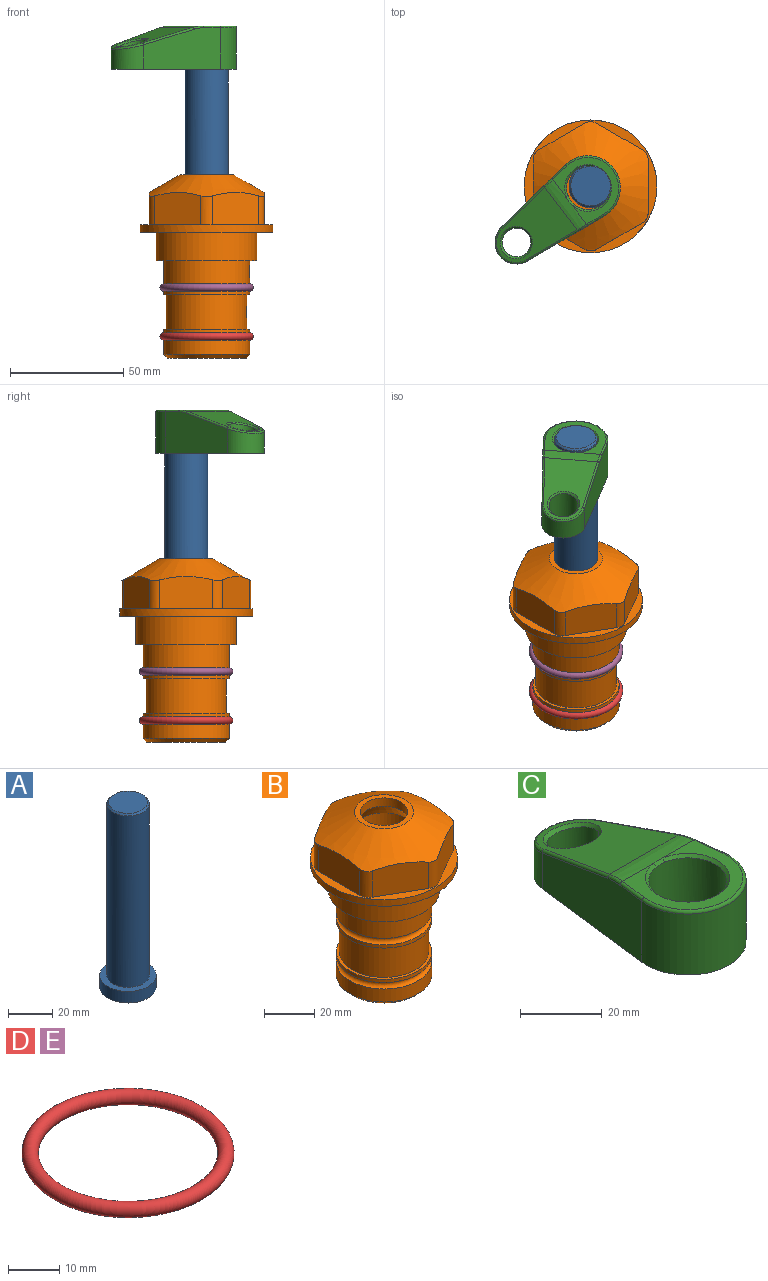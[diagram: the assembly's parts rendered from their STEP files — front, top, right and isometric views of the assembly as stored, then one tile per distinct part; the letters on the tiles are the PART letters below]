
ASSEMBLY  parts=5 mates=4
PART A: 6 faces, bbox 25.4x25.4x101.6 mm
  f0: plane 17.46x17.46mm, normal (0,0,1), area 239.5mm2, adj f5
  f1: plane 25.4x25.4mm, normal (0,0,-1), area 506.7mm2, adj f2
  f2: cylinder r=12.7mm len=25.4mm, axis (0,0,1), area 506.7mm2, adj f1,f3
  f3: plane 25.4x25.4mm, normal (0,0,1), area 221.7mm2, adj f2,f4
  f4: cylinder r=9.53mm len=94.46mm, axis (0,0,1), area 5653mm2, adj f3,f5
  f5: cone r=8.73mm half-angle=45deg, axis (0,0,-1), area 64.4mm2, adj f0,f4
PART B: 36 faces, bbox 58.7x58.7x81 mm
  f0: cylinder r=17.78mm len=35.56mm, axis (0,0,1), area 1670.8mm2, adj f23,f24,f31
  f1: cylinder r=19.05mm len=38.1mm, axis (0,0,1), area 1191.9mm2, adj f26,f27,f30
  f2: plane 58.66x58.66mm, normal (0,0,-1), area 1150.6mm2, adj f3,f28
  f3: cylinder r=29.33mm len=58.66mm, axis (0,0,-1), area 585.1mm2, adj f2,f4
  f4: plane 58.66x58.66mm, normal (0,0,1), area 475.9mm2, adj f3,f5,f6,f7,f8,f9,f10,f11
  f5: plane 20.32x14.34mm, normal (-0.5,0.87,0), area 324.4mm2, adj f4,f15,f16,f17
  f6: plane 20.32x14.34mm, normal (0.5,0.87,0), area 324.4mm2, adj f4,f14,f15,f17
  f7: plane 23.48x14.34mm, normal (1,0,0), area 324.4mm2, adj f4,f13,f14,f17
  f8: plane 20.32x14.34mm, normal (0.5,-0.87,0), area 324.4mm2, adj f4,f12,f13,f17
  f9: plane 20.32x14.34mm, normal (-0.5,-0.87,0), area 324.4mm2, adj f4,f11,f12,f17
  f10: plane 23.48x14.34mm, normal (-1,0,0), area 324.4mm2, adj f4,f11,f16,f17
  f11: cylinder r=5.08mm len=12.85mm, axis (0,0,-1), area 67.2mm2, adj f4,f9,f10,f17
  f12: cylinder r=5.08mm len=12.85mm, axis (0,0,-1), area 67.2mm2, adj f4,f8,f9,f17
  f13: cylinder r=5.08mm len=12.85mm, axis (0,0,-1), area 67.2mm2, adj f4,f7,f8,f17
  f14: cylinder r=5.08mm len=12.85mm, axis (0,0,-1), area 67.2mm2, adj f4,f6,f7,f17
  f15: cylinder r=5.08mm len=12.85mm, axis (0,0,-1), area 67.2mm2, adj f4,f5,f6,f17
  f16: cylinder r=5.08mm len=12.85mm, axis (0,0,-1), area 67.2mm2, adj f4,f5,f10,f17
  f17: cone r=11.73mm half-angle=60deg, axis (0,0,-1), area 2071.8mm2, adj f5,f6,f7,f8,f9,f10,f11,f12
  f18: plane 23.46x23.46mm, normal (0,0,1), area 147.4mm2, adj f17,f35
  f19: plane 34.93x34.93mm, normal (0,0,-1), area 958mm2, adj f29
  f20: cylinder r=19.05mm len=38.1mm, axis (0,0,1), area 760.1mm2, adj f21,f29
  f21: torus R=19.05mm, axis (0,0,1), area 565.3mm2, adj f20,f22
  f22: cylinder r=19.05mm len=38.1mm, axis (0,0,1), area 190mm2, adj f21,f23
  f23: plane 38.1x38.1mm, normal (0,0,1), area 146.9mm2, adj f0,f22
  f24: plane 38.1x38.1mm, normal (0,0,-1), area 146.9mm2, adj f0,f25
  f25: cylinder r=19.05mm len=38.1mm, axis (0,0,1), area 190mm2, adj f24,f26
  f26: torus R=19.05mm, axis (0,0,1), area 565.3mm2, adj f1,f25
  f27: plane 44.45x44.45mm, normal (0,0,-1), area 411.7mm2, adj f1,f28
  f28: cylinder r=22.23mm len=44.45mm, axis (0,0,1), area 1773.5mm2, adj f2,f27
  f29: cone r=19.05mm half-angle=45deg, axis (0,0,1), area 257.5mm2, adj f19,f20
  f30: cylinder r=3.17mm len=6.75mm, axis (-1,0,0), area 128mm2, adj f1,f33
  f31: cylinder r=3.17mm len=6.35mm, axis (-1,0,0), area 102.5mm2, adj f0,f33
  f32: plane 25.4x25.4mm, normal (0,0,1), area 506.7mm2, adj f33
  f33: cylinder r=12.7mm len=66.42mm, axis (0,0,-1), area 5236.2mm2, adj f30,f31,f32,f34
  f34: cone r=9.53mm half-angle=30deg, axis (0,0,-1), area 443.4mm2, adj f33,f35
  f35: cylinder r=9.53mm len=19.05mm, axis (0,0,-1), area 240.9mm2, adj f18,f34
PART C: 31 faces, bbox 31.7x65.5x19.8 mm
  f0: plane 39.12x18.26mm, normal (0.99,0.12,0), area 612.2mm2, adj f1,f4,f7,f11,f13,f15
  f1: cylinder r=9.53mm len=18.91mm, axis (0,0,-1), area 296.1mm2, adj f0,f2,f7,f17
  f2: plane 39.12x18.26mm, normal (-0.99,0.12,0), area 612.2mm2, adj f1,f4,f7,f12,f14,f16
  f3: cylinder r=6.35mm len=12.7mm, axis (0,0,-1), area 362.4mm2, adj f7,f18
  f4: cylinder r=14.29mm len=28.58mm, axis (0,0,-1), area 882.2mm2, adj f0,f2,f7,f10
  f5: cylinder r=9.53mm len=19.05mm, axis (0,0,-1), area 1092.6mm2, adj f7,f19,f20
  f6: plane 26.99x23.69mm, normal (0,0,1), area 216.2mm2, adj f9,f10,f11,f12,f19
  f7: plane 63.5x28.58mm, normal (0,0,-1), area 661.8mm2, adj f0,f1,f2,f3,f4,f5,f22,f23
  f8: plane 33.52x23.6mm, normal (0,0.26,0.97), area 486mm2, adj f9,f15,f16,f17,f18
  f9: cylinder r=19.05mm len=24.72mm, axis (1,0,0), area 120.4mm2, adj f6,f8,f13,f14,f20
  f10: torus R=13.49mm, axis (0,0,1), area 59mm2, adj f4,f6,f11,f12
  f11: cylinder r=0.79mm len=8.67mm, axis (0.12,-0.99,0), area 10.8mm2, adj f0,f6,f10,f13
  f12: cylinder r=0.79mm len=8.67mm, axis (0.12,0.99,0), area 10.8mm2, adj f2,f6,f10,f14
  f13: bspline ~4.95x1.42mm, area 6.1mm2, adj f0,f9,f11,f15
  f14: bspline ~4.95x1.42mm, area 6.1mm2, adj f2,f9,f12,f16
  f15: cylinder r=0.79mm len=25.95mm, axis (0.12,-0.96,0.26), area 32.9mm2, adj f0,f8,f13,f17
  f16: cylinder r=0.79mm len=25.95mm, axis (0.12,0.96,-0.26), area 32.9mm2, adj f2,f8,f14,f17
  f17: bspline ~18.91x8.38mm, area 30mm2, adj f1,f8,f15,f16
  f18: bspline ~14.29x14.29mm, area 48.3mm2, adj f3,f8
  f19: cone r=9.53mm half-angle=45deg, axis (0,0,1), area 66.5mm2, adj f5,f6,f20
  f20: bspline ~3.22x0.96mm, area 3.5mm2, adj f5,f9,f19
  f21: plane 2.75x2.72mm, normal (0,0,-1), area 2.9mm2, adj f23,f25,f28
  f22: plane 23.05x15.88mm, normal (-0.99,-0.12,0), area 323.6mm2, adj f7,f25,f26,f27,f28,f29
  f23: plane 23.05x15.88mm, normal (0.99,-0.12,0), area 323.6mm2, adj f7,f21,f25,f27,f28,f30
  f24: cylinder r=9.53mm len=10.69mm, axis (0,0,-1), area 114.7mm2, adj f7,f27,f29,f30
  f25: cylinder r=12.7mm len=20.59mm, axis (0,0,-1), area 381.1mm2, adj f7,f21,f22,f23,f26,f28
  f26: plane 2.75x2.72mm, normal (0,0,-1), area 2.9mm2, adj f22,f25,f28
  f27: plane 19.72x18.37mm, normal (0,-0.26,-0.97), area 291.8mm2, adj f22,f23,f24,f28,f29,f30
  f28: cylinder r=15.88mm len=19.92mm, axis (1,0,0), area 54.8mm2, adj f21,f22,f23,f25,f26,f27
  f29: cylinder r=1.59mm len=11mm, axis (0,0,-1), area 34.7mm2, adj f7,f22,f24,f27
  f30: cylinder r=1.59mm len=11mm, axis (0,0,-1), area 34.7mm2, adj f7,f23,f24,f27
PART D: 1 faces, bbox 44.7x44.7x3.2 mm
  f0: torus R=19.05mm, axis (0,0,1), area 1193.9mm2
PART E: same geometry as D
PLACE A rot(axis=(0,0,1),127.3deg) t=(0,0,27.55)mm
PLACE B at identity fixed
PLACE C rot(axis=(0,0,1),127.3deg) t=(-1.14,-0.86,27.55)mm
PLACE D t=(0,0,-21.59)mm
PLACE E at identity
MATE fastened B.f0 <-> E.f0  axis (0,0,1) through (0,0,-24.51)mm
MATE fastened A.f2 <-> C.f6  axis (0,0,1) through (0,0,91.05)mm
MATE cylindrical B.f0 <-> A.f2  axis (0,0,1) through (0,0,-50.55)mm
MATE fastened B.f0 <-> D.f0  axis (0,0,1) through (0,0,-46.1)mm
